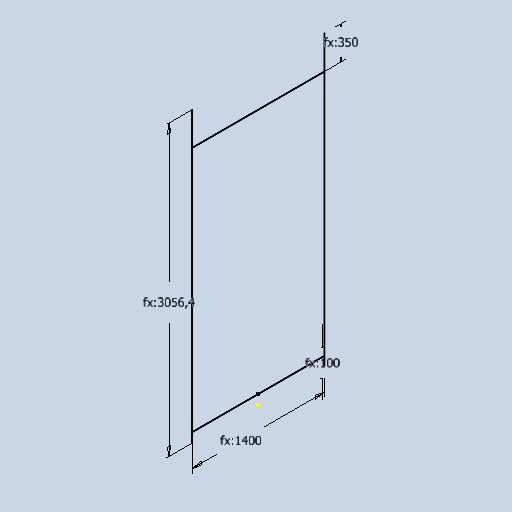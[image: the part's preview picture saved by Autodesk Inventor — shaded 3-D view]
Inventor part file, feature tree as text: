
AUTODESK INVENTOR PART (.ipt)
format: ipt  version: 2025 (Build 290162010, 162A)  size: 86,016 bytes
history: native  units: mm
features: sketch x1
ambient origin geometry x8: Origin, YZ Plane, XZ Plane, XY Plane, X Axis, Y Axis, Z Axis, Center Point
feature tree (1):
  sketch  "Sketch2"  dims[d4=3056.399996mm d5=1400.0mm d6=350.0mm d7=100.0mm]
